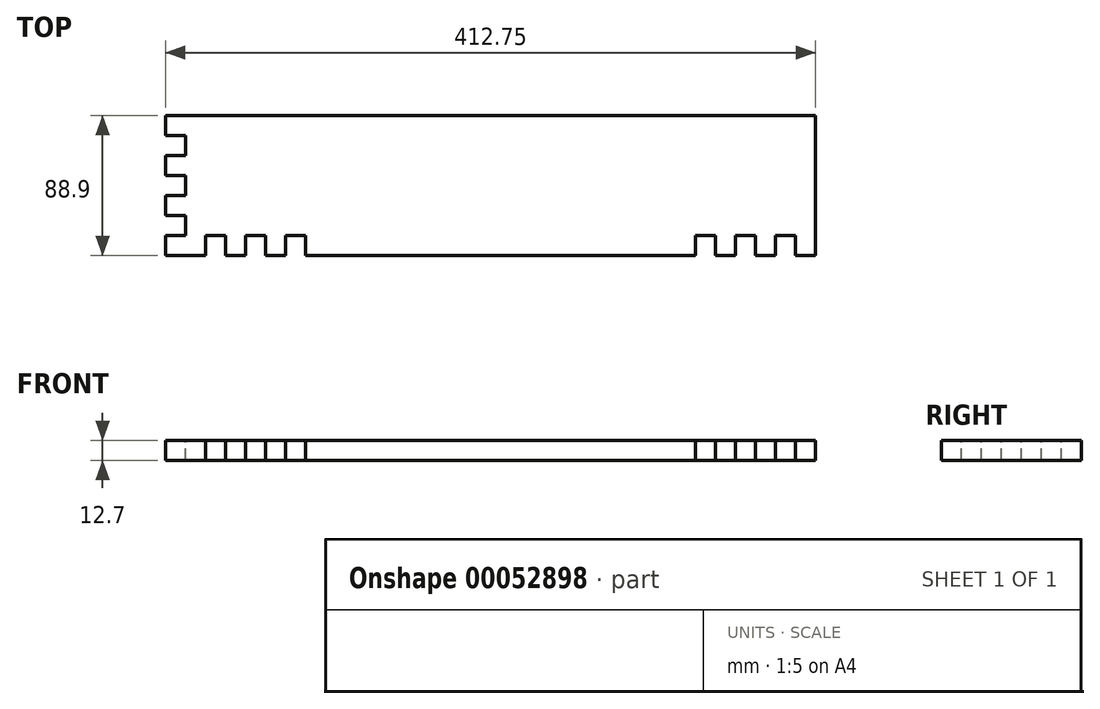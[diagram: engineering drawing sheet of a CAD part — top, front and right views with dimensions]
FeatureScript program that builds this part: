
annotation { "Feature Type Name" : "Feature", "Feature Type Description" : "" }
export const myFeature = defineFeature(function(context is Context, id is Id, definition is map)
    precondition{}
    {
        {
            var Q0;
            Q0=qCreatedBy(makeId("Top.planeOp"),FACE);
            var sketch = newSketch(context, id + "F0", { "sketchPlane" : qUnion([Q0])});
            skLineSegment(sketch, "E0.bottom", {"start": v(0, 0) * mm, "end": v(412.75, 0) * mm});
            skLineSegment(sketch, "E0.top", {"start": v(0, 88.9) * mm, "end": v(412.75, 88.9) * mm});
            skLineSegment(sketch, "E0.left", {"start": v(0, 0) * mm, "end": v(0, 88.9) * mm});
            skLineSegment(sketch, "E0.right", {"start": v(412.75, 0) * mm, "end": v(412.75, 88.9) * mm});
            skSolve(sketch);
        }
        {
            var Q0;
            Q0=qSketchRegion(id+"F0",true);
            extrude(context, id + "F1", {"entities" : qUnion([Q0]), "depth" : 12.7 * mm});
        }
        {
            var Q0;
            Q0=makeQuery(id+"F1.opExtrude","CAP_FACE",FACE,{"disambiguationData":[OSD([sQuery(id+"F0.wireOp",EDGE,"E0.bottom"),sQuery(id+"F0.wireOp",EDGE,"E0.top"),sQuery(id+"F0.wireOp",EDGE,"E0.left"),sQuery(id+"F0.wireOp",EDGE,"E0.right")])],"isStart":false});
            var sketch = newSketch(context, id + "F2", { "sketchPlane" : qUnion([Q0])});
            skLineSegment(sketch, "E1.bottom", {"start": v(0, 12.7) * mm, "end": v(12.7, 12.7) * mm});
            skLineSegment(sketch, "E1.top", {"start": v(0, 25.4) * mm, "end": v(12.7, 25.4) * mm});
            skLineSegment(sketch, "E1.left", {"start": v(0, 12.7) * mm, "end": v(0, 25.4) * mm});
            skLineSegment(sketch, "E1.right", {"start": v(12.7, 12.7) * mm, "end": v(12.7, 25.4) * mm});
            skLineSegment(sketch, "E2.bottom", {"start": v(0, 63.5) * mm, "end": v(12.7, 63.5) * mm});
            skLineSegment(sketch, "E2.top", {"start": v(0, 76.2) * mm, "end": v(12.7, 76.2) * mm});
            skLineSegment(sketch, "E2.left", {"start": v(0, 63.5) * mm, "end": v(0, 76.2) * mm});
            skLineSegment(sketch, "E2.right", {"start": v(12.7, 63.5) * mm, "end": v(12.7, 76.2) * mm});
            skLineSegment(sketch, "E3.bottom", {"start": v(0, 38.1) * mm, "end": v(12.7, 38.1) * mm});
            skLineSegment(sketch, "E3.top", {"start": v(0, 50.8) * mm, "end": v(12.7, 50.8) * mm});
            skLineSegment(sketch, "E3.left", {"start": v(0, 38.1) * mm, "end": v(0, 50.8) * mm});
            skLineSegment(sketch, "E3.right", {"start": v(12.7, 38.1) * mm, "end": v(12.7, 50.8) * mm});
            skSolve(sketch);
        }
        {
            var Q0;
            Q0=qSketchRegion(id+"F2",true);
            extrude(context, id + "F3", {"entities" : qUnion([Q0]), "operationType" : NewBodyOperationType.REMOVE, "oppositeDirection" : true, "depth" : 25.4 * mm});
        }
        {
            var Q0;
            Q0=makeQuery(id+"F1.opExtrude","CAP_FACE",FACE,{"disambiguationData":[OSD([sQuery(id+"F0.wireOp",EDGE,"E0.bottom"),sQuery(id+"F0.wireOp",EDGE,"E0.top"),sQuery(id+"F0.wireOp",EDGE,"E0.left"),sQuery(id+"F0.wireOp",EDGE,"E0.right")])],"isStart":false});
            var sketch = newSketch(context, id + "F4", { "sketchPlane" : qUnion([Q0])});
            skLineSegment(sketch, "E4.bottom", {"start": v(400.05, 0) * mm, "end": v(387.35, 0) * mm});
            skLineSegment(sketch, "E4.top", {"start": v(400.05, 12.7) * mm, "end": v(387.35, 12.7) * mm});
            skLineSegment(sketch, "E4.left", {"start": v(400.05, 0) * mm, "end": v(400.05, 12.7) * mm});
            skLineSegment(sketch, "E4.right", {"start": v(387.35, 0) * mm, "end": v(387.35, 12.7) * mm});
            skLineSegment(sketch, "E5.bottom", {"start": v(374.65, 0) * mm, "end": v(361.95, 0) * mm});
            skLineSegment(sketch, "E5.top", {"start": v(374.65, 12.7) * mm, "end": v(361.95, 12.7) * mm});
            skLineSegment(sketch, "E5.left", {"start": v(374.65, 0) * mm, "end": v(374.65, 12.7) * mm});
            skLineSegment(sketch, "E5.right", {"start": v(361.95, 0) * mm, "end": v(361.95, 12.7) * mm});
            skLineSegment(sketch, "E6.bottom", {"start": v(349.25, 0) * mm, "end": v(336.55, 0) * mm});
            skLineSegment(sketch, "E6.top", {"start": v(349.25, 12.7) * mm, "end": v(336.55, 12.7) * mm});
            skLineSegment(sketch, "E6.left", {"start": v(349.25, 0) * mm, "end": v(349.25, 12.7) * mm});
            skLineSegment(sketch, "E6.right", {"start": v(336.55, 0) * mm, "end": v(336.55, 12.7) * mm});
            skSolve(sketch);
        }
        {
            var Q0;
            Q0 = qSketchRegion(id + "F4", true);
            extrude(context, id + "F5", {"entities" : qUnion([Q0]), "operationType" : NewBodyOperationType.REMOVE, "oppositeDirection" : true, "depth" : 25.4 * mm});
        }
        {
            var Q0;
            Q0=makeQuery(id+"F1.opExtrude","CAP_FACE",FACE,{"disambiguationData":[OSD([sQuery(id+"F0.wireOp",EDGE,"E0.bottom"),sQuery(id+"F0.wireOp",EDGE,"E0.top"),sQuery(id+"F0.wireOp",EDGE,"E0.left"),sQuery(id+"F0.wireOp",EDGE,"E0.right")])],"isStart":false});
            var sketch = newSketch(context, id + "F6", { "sketchPlane" : qUnion([Q0])});
            skLineSegment(sketch, "E7.bottom", {"start": v(25.4, 0) * mm, "end": v(38.1, 0) * mm});
            skLineSegment(sketch, "E7.top", {"start": v(25.4, 12.7) * mm, "end": v(38.1, 12.7) * mm});
            skLineSegment(sketch, "E7.left", {"start": v(25.4, 0) * mm, "end": v(25.4, 12.7) * mm});
            skLineSegment(sketch, "E7.right", {"start": v(38.1, 0) * mm, "end": v(38.1, 12.7) * mm});
            skLineSegment(sketch, "E8.bottom", {"start": v(50.8, 0) * mm, "end": v(63.5, 0) * mm});
            skLineSegment(sketch, "E8.top", {"start": v(50.8, 12.7) * mm, "end": v(63.5, 12.7) * mm});
            skLineSegment(sketch, "E8.left", {"start": v(50.8, 0) * mm, "end": v(50.8, 12.7) * mm});
            skLineSegment(sketch, "E8.right", {"start": v(63.5, 0) * mm, "end": v(63.5, 12.7) * mm});
            skLineSegment(sketch, "E9.bottom", {"start": v(76.2, 0) * mm, "end": v(88.9, 0) * mm});
            skLineSegment(sketch, "E9.top", {"start": v(76.2, 12.7) * mm, "end": v(88.9, 12.7) * mm});
            skLineSegment(sketch, "E9.left", {"start": v(76.2, 0) * mm, "end": v(76.2, 12.7) * mm});
            skLineSegment(sketch, "E9.right", {"start": v(88.9, 0) * mm, "end": v(88.9, 12.7) * mm});
            skSolve(sketch);
        }
        {
            var Q0;
            Q0 = qSketchRegion(id + "F6", true);
            extrude(context, id + "F7", {"entities" : qUnion([Q0]), "operationType" : NewBodyOperationType.REMOVE, "oppositeDirection" : true, "depth" : 25.4 * mm});
        }
    });
